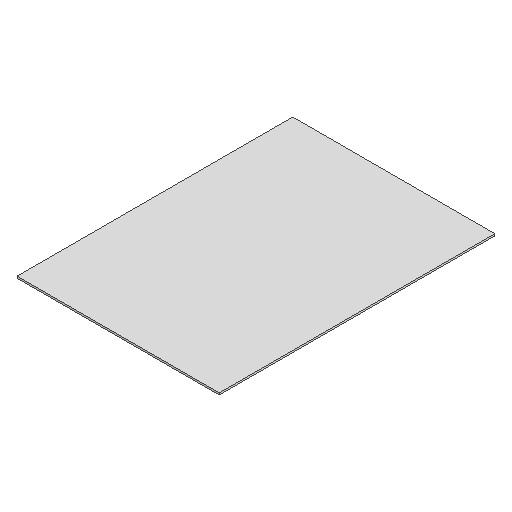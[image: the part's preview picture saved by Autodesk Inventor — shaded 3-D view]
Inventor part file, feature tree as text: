
AUTODESK INVENTOR PART (.ipt)
format: ipt  version: 2025.1 (Build 291241000, 241)  size: 77,824 bytes
history: native  units: mm
features: other x1, extrude x1, sketch x1
ambient origin geometry x8: Origin, YZ Plane, XZ Plane, XY Plane, X Axis, Y Axis, Z Axis, Center Point
bodies: Body1 (feature_tree)
feature tree (3):
  other  "Bryła1"
  extrude  "Wyciągnięcie proste1"  Depth=1100.0mm
  sketch  "Szkic1"
